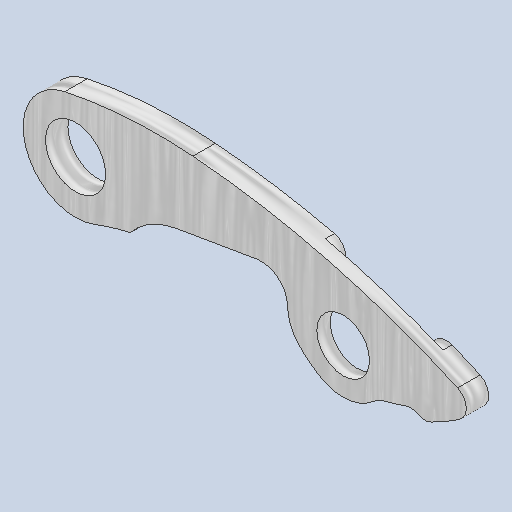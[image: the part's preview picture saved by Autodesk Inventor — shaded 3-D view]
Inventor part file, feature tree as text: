
AUTODESK INVENTOR PART (.ipt)
format: ipt  version: 2023 (Build 270158030, 158C)  size: 233,472 bytes
history: native  units: mm
features: other x3, sketch x2
ambient origin geometry x8: Origin, YZ Plane, XZ Plane, XY Plane, X Axis, Y Axis, Z Axis, Center Point
bodies: Solid4 (feature_tree)
feature tree (5):
  other  "揺動節.ipt"
  other  "Solid4::揺動節.ipt"
  other  "TaggingFeature1"
  sketch  "Sketch1"  dims[d0=10.0mm]
  sketch  "Sketch4"
